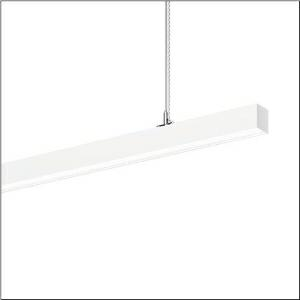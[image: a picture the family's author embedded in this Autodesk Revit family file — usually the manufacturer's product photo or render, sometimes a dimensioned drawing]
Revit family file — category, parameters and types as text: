
# Revit family: silica_r__21_51mx30db35wb_0444
name_source: partatom
category: Lighting Fixtures
units: mm (PartAtom-declared; Revit-internal decimal feet)

## family parameters
Cut with Voids When Loaded = No
Host = Face
Light Source = No
Part Type = Normal
Room Calculation Point = No
Round Connector Dimension = Use Diameter
Shared = No

## types (1)
- --- (1 x LED, 5260 lm, 34.1 W, 3000K)
    Apparent Load = 34 VA
    CIE Flux Codes = 47 79 96 57 100
    Color Rendering = 80
    Color Temperature = 3000K
    Default Elevation = 1800 mm
    Description = Silica® 21, office luminaire, primary optical cover: cover, of PMMA, opal, light emission: direct/indirect distribution, primary light characteristic: symmetric, installation type: suspended mounting, LED, rated luminous flux: 5.260lm, luminous efficacy: 154lm/W, light colour: 830, colour temperature: 3000K, with terminal, 3+2-pole, max. 2.5mm², mains connection: 220..240V, AC, 50/60Hz, rated input power: 34.1W, luminaire housing, of aluminium, traffic white (RAL 9016), length: 1.504mm, width: 53mm, height: 53mm, protection rating (complete): IP20, insulation class (complete): insulation class I (protective earthing), certification: CE, permissible operating ambient temperature: 0..+35°C, standard: EN 50419, packaging unit: 1 piece
    Height = 53 mm
    Lamp = 1 x LED
    Lamp Light Flux = 5260 lm
    Lamp Power = 34.1 W
    Lamp count = 1
    Length = 1504 mm
    Luminous efficacy = 154 lm/W
    Manufacturer = Siteco
    ModVariant = No
    Model = 51MX30DB35WB
    Mounting Place = Ceiling
    Mounting Type = Pendant
    Number of Poles = 1
    OnlyDefault = Yes
    Power Factor = 1
    Product Name = Silica® 21
    Product group = office luminaire | ceiling pendant
    ProductGroupID = 905
    Protection Class = Protection class I
    Protection Degree = IP 20
    RLX_Detail_Level = 1
    RlxData = <blob elided: 21449 chars, md5=ecca662b>
    Socket = socket
    Standby Power = 0 W
    System Light Flux = 5260 lm
    System Power = 34 W
    Type Comments = factory setting: luminous flux: 100 % | dim-lin: 254 | 233 mA
    Type Image = l_1251642.jpg
    URL = http://relux.com
    VarID = @adj_025255
    Voltage = 0 V
    Weight = 0.00 kg
    Width = 53 mm

## geometry (parser evidence)
native form markers: Blend x4, Sweep x12
no freeform markers — native parametric forms only
